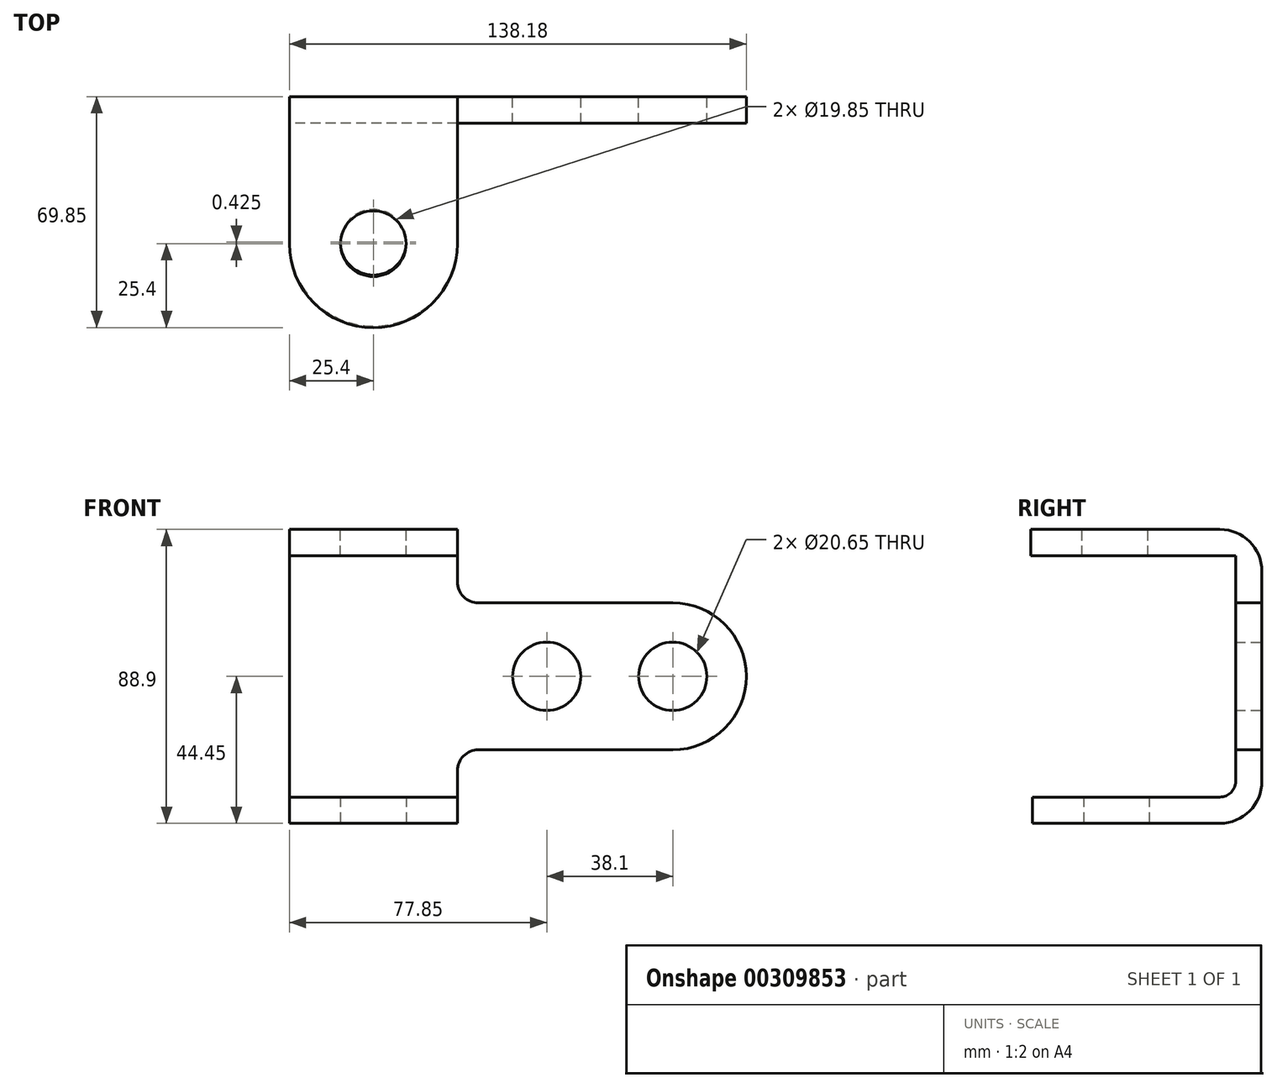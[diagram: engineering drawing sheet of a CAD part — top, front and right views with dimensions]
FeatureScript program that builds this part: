
annotation { "Feature Type Name" : "Feature", "Feature Type Description" : "" }
export const myFeature = defineFeature(function(context is Context, id is Id, definition is map)
    precondition{}
    {
        {
            var Q0;
            Q0=qCreatedBy(makeId("Front.planeOp"),FACE);
            var sketch = newSketch(context, id + "F0", { "sketchPlane" : qUnion([Q0])});
            skLineSegment(sketch, "E0", {"start": v(0, 0) * mm, "end": v(0, 88.9) * mm});
            skLineSegment(sketch, "E1", {"start": v(0, 88.9) * mm, "end": v(50.8, 88.9) * mm});
            skLineSegment(sketch, "E2", {"start": v(0, 0) * mm, "end": v(50.8, 0) * mm});
            skLineSegment(sketch, "E3", {"start": v(0, 44.45) * mm, "end": v(155.7, 44.45) * mm, "construction": true});
            skCircle(sketch, "E4", {"center": v(77.85, 44.45) * mm, "radius": 10.33 * mm});
            skCircle(sketch, "E5", {"center": v(115.95, 44.45) * mm, "radius": 10.33 * mm});
            skLineSegment(sketch, "E6", {"start": v(115.95, 82.5) * mm, "end": v(115.95, -2.02) * mm, "construction": true});
            skArc(sketch, "E7", {"start": v(115.95, 66.68) * mm, "mid": v(138.18, 44.45) * mm, "end": v(115.95, 22.23) * mm});
            skLineSegment(sketch, "E8", {"start": v(115.95, 66.68) * mm, "end": v(65.15, 66.68) * mm});
            skLineSegment(sketch, "E9", {"start": v(115.95, 22.23) * mm, "end": v(65.15, 22.22) * mm});
            skLineSegment(sketch, "E10", {"start": v(50.8, 0) * mm, "end": v(50.8, 15.87) * mm});
            skLineSegment(sketch, "E11", {"start": v(50.8, 88.9) * mm, "end": v(50.8, 73.03) * mm});
            skLineSegment(sketch, "E12", {"start": v(57.15, 66.68) * mm, "end": v(65.15, 66.68) * mm});
            skLineSegment(sketch, "E13", {"start": v(57.15, 22.22) * mm, "end": v(65.15, 22.22) * mm});
            skPoint(sketch, "E14.visualSharp", {"position": v(50.8, 66.68) * mm});
            skArc(sketch, "E14.filletArc", {"start": v(50.8, 73.03) * mm, "mid": v(52.66, 68.53) * mm, "end": v(57.15, 66.68) * mm});
            skPoint(sketch, "E15.visualSharp", {"position": v(50.8, 22.22) * mm});
            skArc(sketch, "E15.filletArc", {"start": v(57.15, 22.22) * mm, "mid": v(52.66, 20.37) * mm, "end": v(50.8, 15.87) * mm});
            skSolve(sketch);
        }
        {
            var Q0;
            Q0 = qSketchRegion(id + "F0", true);
            extrude(context, id + "F1", {"entities" : qUnion([Q0]), "depth" : 7.96 * mm});
        }
        {
            var Q0;
            Q0=qCreatedBy(makeId("Top.planeOp"),FACE);
            var sketch = newSketch(context, id + "F2", { "sketchPlane" : qUnion([Q0])});
            skCircle(sketch, "E16", {"center": v(25.4, -44.03) * mm, "radius": 9.92 * mm});
            skArc(sketch, "E17", {"start": v(0, -44.03) * mm, "mid": v(25.4, -69.43) * mm, "end": v(50.8, -44.03) * mm});
            skLineSegment(sketch, "E18", {"start": v(0, 0) * mm, "end": v(0, -44.03) * mm});
            skLineSegment(sketch, "E19", {"start": v(50.8, -44.03) * mm, "end": v(50.8, 0) * mm});
            skLineSegment(sketch, "E20", {"start": v(0, 0) * mm, "end": v(50.8, 0) * mm});
            skSolve(sketch);
        }
        {
            var Q0;
            Q0=makeQuery(id+"F2.imprint","IMPRINT",FACE,{"disambiguationData":[TD([[makeQuery(id+"F2.imprint","IMPRINT",EDGE,{"derivedFrom":sQuery(id+"F2.wireOp",EDGE,"E16")}),-1.0]])]});
            extrude(context, id + "F3", {"entities" : qUnion([Q0]), "operationType" : NewBodyOperationType.ADD, "depth" : 7.94 * mm});
        }
        {
            var Q0;
            Q0=makeQuery(id+"F1.opExtrude","SWEPT_FACE",FACE,{"disambiguationData":[OSD([sQuery(id+"F0.wireOp",EDGE,"E1")])]});
            var sketch = newSketch(context, id + "F4", { "sketchPlane" : qUnion([Q0])});
            skLineSegment(sketch, "E21", {"start": v(50.8, 0) * mm, "end": v(25.4, 0) * mm});
            skCircle(sketch, "E22", {"center": v(25.4, -44.45) * mm, "radius": 9.92 * mm});
            skLineSegment(sketch, "E23", {"start": v(50.8, 0) * mm, "end": v(50.8, -44.45) * mm});
            skLineSegment(sketch, "E24", {"start": v(50.8, 0) * mm, "end": v(0, 0) * mm});
            skLineSegment(sketch, "E25", {"start": v(0, 0) * mm, "end": v(0, -44.45) * mm});
            skArc(sketch, "E26", {"start": v(0, -44.45) * mm, "mid": v(25.4, -69.85) * mm, "end": v(50.8, -44.45) * mm});
            skSolve(sketch);
        }
        {
            var Q0;
            Q0=makeQuery(id+"F4.imprint","IMPRINT",FACE,{"disambiguationData":[TD([[makeQuery(id+"F4.imprint","IMPRINT",EDGE,{"derivedFrom":sQuery(id+"F4.wireOp",EDGE,"E22")}),-1.0]])]});
            extrude(context, id + "F5", {"entities" : qUnion([Q0]), "operationType" : NewBodyOperationType.ADD, "oppositeDirection" : true, "depth" : 7.96 * mm});
        }
        {
            var Q0;
            Q0=makeQuery(id+"F1.opExtrude","CAP_EDGE",EDGE,{"disambiguationData":[OSD([sQuery(id+"F0.wireOp",EDGE,"E2")])],"isStart":true});
            var Q1;
            Q1=makeQuery(id+"F1.opExtrude","CAP_EDGE",EDGE,{"disambiguationData":[OSD([sQuery(id+"F0.wireOp",EDGE,"E1")])],"isStart":true});
            fillet(context, id + "F6", {"entities" : qUnion([Q0, Q1]), "radius" : 12.7 * mm, "tangentPropagation" : true, "allowEdgeOverflow" : false});
        }
        {
            var Q0;
            Q0=makeQuery(id+"F3.boolean.opBoolean","INTERSECT",EDGE,{"derivedFrom":[makeQuery(id+"F1.opExtrude","CAP_FACE",FACE,{"disambiguationData":[OSD([sQuery(id+"F0.wireOp",EDGE,"E0"),sQuery(id+"F0.wireOp",EDGE,"E1"),sQuery(id+"F0.wireOp",EDGE,"E2"),sQuery(id+"F0.wireOp",EDGE,"E4"),sQuery(id+"F0.wireOp",EDGE,"E5"),sQuery(id+"F0.wireOp",EDGE,"E7"),sQuery(id+"F0.wireOp",EDGE,"E8"),sQuery(id+"F0.wireOp",EDGE,"E9"),sQuery(id+"F0.wireOp",EDGE,"E10"),sQuery(id+"F0.wireOp",EDGE,"E11"),sQuery(id+"F0.wireOp",EDGE,"E12"),sQuery(id+"F0.wireOp",EDGE,"E13"),sQuery(id+"F0.wireOp",EDGE,"E14.filletArc"),sQuery(id+"F0.wireOp",EDGE,"E15.filletArc")])],"isStart":false}),makeQuery(id+"F3.opExtrude","CAP_FACE",FACE,{"disambiguationData":[OSD([sQuery(id+"F2.wireOp",EDGE,"E16"),sQuery(id+"F2.wireOp",EDGE,"E17"),sQuery(id+"F2.wireOp",EDGE,"E18"),sQuery(id+"F2.wireOp",EDGE,"E19"),sQuery(id+"F2.wireOp",EDGE,"E20")])],"isStart":false})]});
            var Q1;
            Q1=makeQuery(id+"F5.opExtrude","CAP_EDGE",EDGE,{"disambiguationData":[OSD([sQuery(id+"F0.wireOp",EDGE,"E1")])],"isStart":false});
            fillet(context, id + "F7", {"entities" : qUnion([Q0, Q1]), "radius" : 4.76 * mm, "tangentPropagation" : true, "allowEdgeOverflow" : false});
        }
    });
